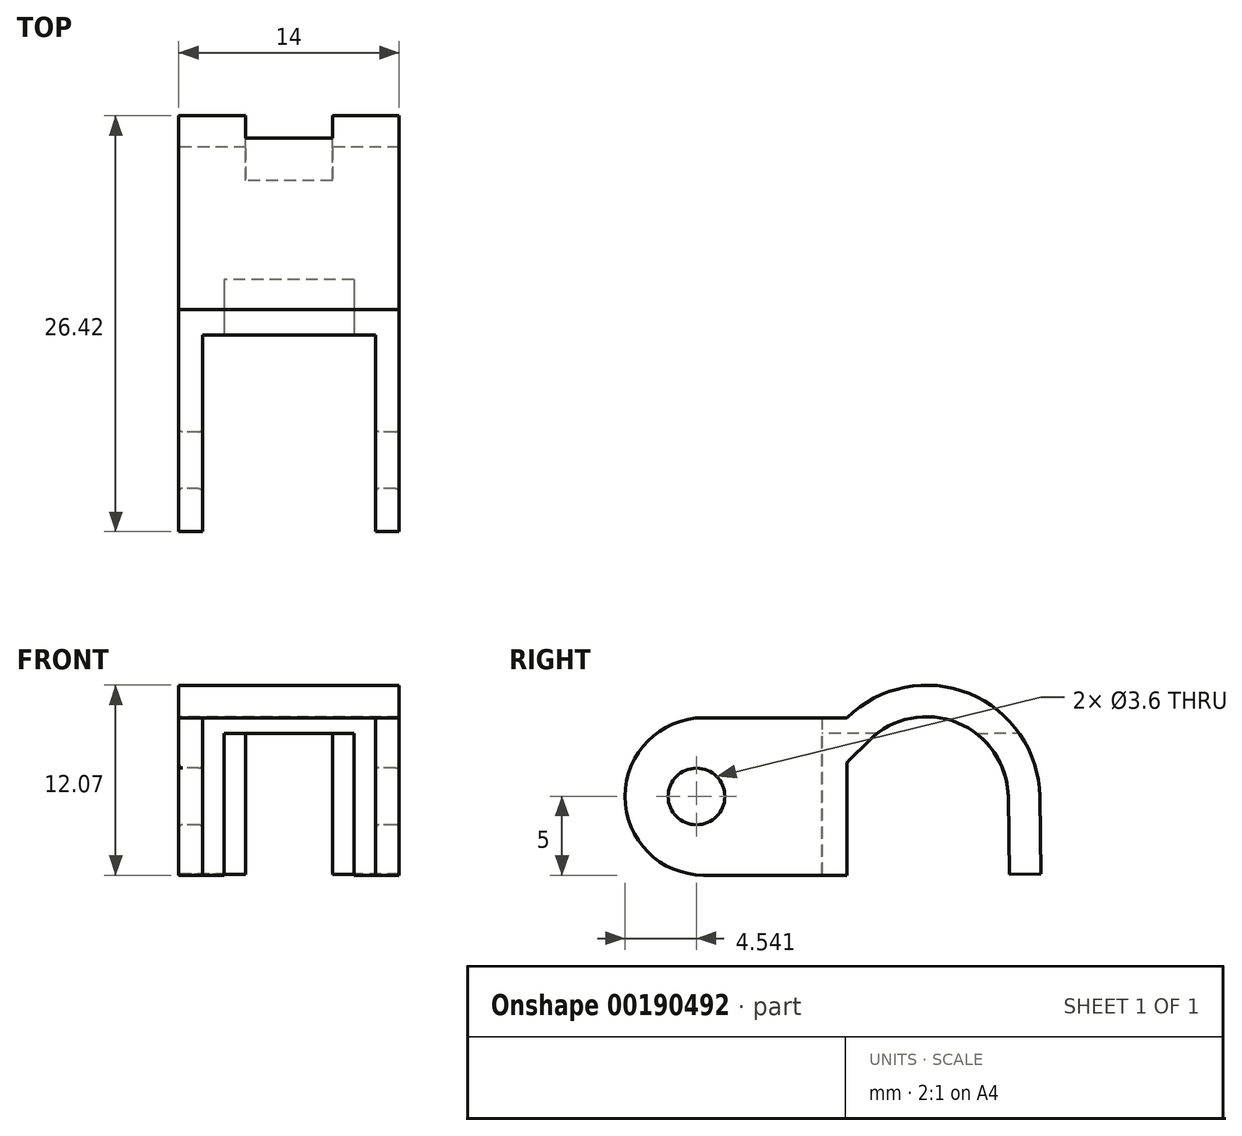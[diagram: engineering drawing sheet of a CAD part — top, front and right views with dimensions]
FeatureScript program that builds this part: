
annotation { "Feature Type Name" : "Feature", "Feature Type Description" : "" }
export const myFeature = defineFeature(function(context is Context, id is Id, definition is map)
    precondition{}
    {
        {
            var Q0;
            Q0=qCreatedBy(makeId("Right.planeOp"),FACE);
            var sketch = newSketch(context, id + "F0", { "sketchPlane" : qUnion([Q0])});
            skLineSegment(sketch, "E0", {"start": v(48.18, 0) * mm, "end": v(-52.58, 0) * mm, "construction": true});
            skLineSegment(sketch, "E1", {"start": v(0, -5) * mm, "end": v(-9.11, -5) * mm});
            skLineSegment(sketch, "E2.MirrorCS", {"start": v(0, 5) * mm, "end": v(-9.11, 5) * mm});
            skArc(sketch, "E3", {"start": v(-9.11, 5) * mm, "mid": v(-14.11, 0) * mm, "end": v(-9.11, -5) * mm});
            skCircle(sketch, "E4", {"center": v(-9.57, 0) * mm, "radius": 1.8 * mm});
            skArc(sketch, "E5", {"start": v(12.23, 0) * mm, "mid": v(7.76, 6.53) * mm, "end": v(0, 5) * mm});
            skLineSegment(sketch, "E6", {"start": v(12.23, 0) * mm, "end": v(12.31, -4.9) * mm});
            skArc(sketch, "E7.0", {"start": v(10.23, -0.03) * mm, "mid": v(7, 4.68) * mm, "end": v(1.4, 3.58) * mm});
            skLineSegment(sketch, "E7.1", {"start": v(10.23, -0.03) * mm, "end": v(10.31, -4.94) * mm});
            skLineSegment(sketch, "E8", {"start": v(1.4, 3.58) * mm, "end": v(0, 2.2) * mm});
            skLineSegment(sketch, "E9", {"start": v(0, -5) * mm, "end": v(0, 2.2) * mm});
            skLineSegment(sketch, "E10", {"start": v(10.31, -4.94) * mm, "end": v(12.31, -4.9) * mm});
            skSolve(sketch);
        }
        {
            var Q0;
            Q0=makeQuery(id+"F0.imprint","IMPRINT",FACE,{"disambiguationData":[TD([[makeQuery(id+"F0.imprint","IMPRINT",EDGE,{"derivedFrom":sQuery(id+"F0.wireOp",EDGE,"E1")}),-1.0]])]});
            extrude(context, id + "F1", {"entities" : qUnion([Q0]), "depth" : 14 * mm});
        }
        {
            var Q0;
            Q0=makeQuery(id+"F1.opExtrude","SWEPT_FACE",FACE,{"disambiguationData":[OSD([sQuery(id+"F0.wireOp",EDGE,"E6")])]});
            var sketch = newSketch(context, id + "F2", { "sketchPlane" : qUnion([Q0])});
            skLineSegment(sketch, "E11.bottom", {"start": v(-9.75, 3.87) * mm, "end": v(-4.25, 3.87) * mm});
            skLineSegment(sketch, "E11.top", {"start": v(-9.75, -14.1) * mm, "end": v(-4.25, -14.1) * mm});
            skLineSegment(sketch, "E11.left", {"start": v(-9.75, 3.87) * mm, "end": v(-9.75, -14.1) * mm});
            skLineSegment(sketch, "E11.right", {"start": v(-4.25, 3.87) * mm, "end": v(-4.25, -14.1) * mm});
            skPoint(sketch, "E11.middle", {"position": v(-7, -5.11) * mm});
            skSolve(sketch);
        }
        {
            var Q0;
            {var subQ0=sQuery(id+"F2.wireOp",EDGE,"E11.bottom");Q0=makeQuery(id+"F2.imprint","IMPRINT",FACE,{"disambiguationData":[TD([[makeQuery(id+"F2.imprint","IMPRINT",EDGE,{"derivedFrom":subQ0}),-1.0]])]});}
            var Q1;
            {var subQ0=sQuery(id+"F2.wireOp",EDGE,"E11.left");var subQ1=sQuery(id+"F0.wireOp",EDGE,"E6");var subQ2=makeQuery(id+"F1.opExtrude","SWEPT_EDGE",EDGE,{"disambiguationData":[OSD([sQuery(id+"F0.wireOp",EDGE,"E5"),subQ1])]});var subQ3=makeQuery(id+"F2.imprint","INTERSECT",VERTEX,{"derivedFrom":[subQ2,subQ0]});Q1=makeQuery(id+"F2.imprint","IMPRINT",FACE,{"disambiguationData":[TD([[makeQuery(id+"F2.imprint","IMPRINT",EDGE,{"disambiguationData":[TD([[subQ3,-1.0]])],"derivedFrom":subQ0}),1.0]])]});}
            extrude(context, id + "F3", {"entities" : qUnion([Q0, Q1]), "operationType" : NewBodyOperationType.REMOVE, "oppositeDirection" : true, "depth" : 5 * mm});
        }
        {
            var Q0;
            Q0=makeQuery(id+"F1.opExtrude","SWEPT_FACE",FACE,{"disambiguationData":[OSD([sQuery(id+"F0.wireOp",EDGE,"E1")])]});
            var sketch = newSketch(context, id + "F4", { "sketchPlane" : qUnion([Q0])});
            skLineSegment(sketch, "E12.bottom", {"start": v(12.5, 1.61) * mm, "end": v(1.5, 1.61) * mm});
            skLineSegment(sketch, "E12.top", {"start": v(12.5, 16.61) * mm, "end": v(1.5, 16.61) * mm});
            skLineSegment(sketch, "E12.left", {"start": v(12.5, 1.61) * mm, "end": v(12.5, 16.61) * mm});
            skLineSegment(sketch, "E12.right", {"start": v(1.5, 1.61) * mm, "end": v(1.5, 16.61) * mm});
            skPoint(sketch, "E12.middle", {"position": v(7, 9.11) * mm});
            skSolve(sketch);
        }
        {
            var Q0;
            {var subQ0=sQuery(id+"F4.wireOp",EDGE,"E12.top");Q0=makeQuery(id+"F4.imprint","IMPRINT",FACE,{"disambiguationData":[TD([[makeQuery(id+"F4.imprint","IMPRINT",EDGE,{"derivedFrom":subQ0}),1.0]])]});}
            var Q1;
            {var subQ0=sQuery(id+"F4.wireOp",EDGE,"E12.left");var subQ1=sQuery(id+"F0.wireOp",EDGE,"E1");var subQ2=makeQuery(id+"F1.opExtrude","SWEPT_EDGE",EDGE,{"disambiguationData":[OSD([subQ1,sQuery(id+"F0.wireOp",EDGE,"E9")])]});var subQ3=makeQuery(id+"F4.imprint","INTERSECT",VERTEX,{"derivedFrom":[subQ2,subQ0]});Q1=makeQuery(id+"F4.imprint","IMPRINT",FACE,{"disambiguationData":[TD([[makeQuery(id+"F4.imprint","IMPRINT",EDGE,{"disambiguationData":[TD([[subQ3,-1.0]])],"derivedFrom":subQ0}),1.0]])]});}
            extrude(context, id + "F5", {"entities" : qUnion([Q0, Q1]), "operationType" : NewBodyOperationType.REMOVE, "oppositeDirection" : true, "depth" : 12 * mm});
        }
        {
            var Q0;
            Q0=makeQuery(id+"F5.boolean.opBoolean","INTERSECT",EDGE,{"derivedFrom":[makeQuery(id+"F1.opExtrude","SWEPT_FACE",FACE,{"disambiguationData":[OSD([sQuery(id+"F0.wireOp",EDGE,"E3")])]}),makeQuery(id+"F5.opExtrude","CAP_FACE",FACE,{"disambiguationData":[OSD([sQuery(id+"F0.wireOp",EDGE,"E1"),sQuery(id+"F0.wireOp",EDGE,"E9"),sQuery(id+"F4.wireOp",EDGE,"E12.top"),sQuery(id+"F4.wireOp",EDGE,"E12.left"),sQuery(id+"F4.wireOp",EDGE,"E12.right")])],"isStart":false})]});
            var Q1;
            Q1=makeQuery(id+"F5.boolean.opBoolean","INTERSECT",EDGE,{"derivedFrom":[makeQuery(id+"F1.opExtrude","SWEPT_FACE",FACE,{"disambiguationData":[OSD([sQuery(id+"F0.wireOp",EDGE,"E4")])]}),makeQuery(id+"F5.opExtrude","SWEPT_FACE",FACE,{"disambiguationData":[OSD([sQuery(id+"F4.wireOp",EDGE,"E12.right")])]})]});
            var Q2;
            Q2=makeQuery(id+"F5.boolean.opBoolean","INTERSECT",EDGE,{"derivedFrom":[makeQuery(id+"F1.opExtrude","SWEPT_FACE",FACE,{"disambiguationData":[OSD([sQuery(id+"F0.wireOp",EDGE,"E4")])]}),makeQuery(id+"F5.opExtrude","SWEPT_FACE",FACE,{"disambiguationData":[OSD([sQuery(id+"F4.wireOp",EDGE,"E12.left")])]})]});
            var Q3;
            Q3=makeQuery(id+"F1.opExtrude","CAP_EDGE",EDGE,{"disambiguationData":[OSD([sQuery(id+"F0.wireOp",EDGE,"E4")])],"isStart":true});
            var Q4;
            Q4=makeQuery(id+"F1.opExtrude","CAP_EDGE",EDGE,{"disambiguationData":[OSD([sQuery(id+"F0.wireOp",EDGE,"E4")])],"isStart":false});
            var Q5;
            {var subQ0=sQuery(id+"F0.wireOp",EDGE,"E9");var subQ1=sQuery(id+"F0.wireOp",EDGE,"E8");var subQ2=sQuery(id+"F0.wireOp",EDGE,"E1");Q5=makeQuery(id+"F5.boolean.opBoolean","SPLIT",EDGE,{"disambiguationData":[TD([makeQuery(id+"F1.opExtrude","CAP_FACE",FACE,{"disambiguationData":[OSD([subQ2,sQuery(id+"F0.wireOp",EDGE,"E2.MirrorCS"),sQuery(id+"F0.wireOp",EDGE,"E3"),sQuery(id+"F0.wireOp",EDGE,"E4"),sQuery(id+"F0.wireOp",EDGE,"E5"),sQuery(id+"F0.wireOp",EDGE,"E6"),sQuery(id+"F0.wireOp",EDGE,"E7.0"),sQuery(id+"F0.wireOp",EDGE,"E7.1"),subQ1,subQ0,sQuery(id+"F0.wireOp",EDGE,"E10")])],"isStart":true}),makeQuery(id+"F1.opExtrude","SWEPT_FACE",FACE,{"disambiguationData":[OSD([subQ1])]}),makeQuery(id+"F1.opExtrude","SWEPT_FACE",FACE,{"disambiguationData":[OSD([subQ0])]}),makeQuery(id+"F5.opExtrude","SWEPT_FACE",FACE,{"disambiguationData":[OSD([sQuery(id+"F4.wireOp",EDGE,"E12.right")])]}),makeQuery(id+"F5.opExtrude","SWEPT_FACE",FACE,{"disambiguationData":[OSD([subQ2,subQ0])]})])],"derivedFrom":makeQuery(id+"F1.opExtrude","SWEPT_EDGE",EDGE,{"disambiguationData":[OSD([subQ1,subQ0])]})});}
            var Q6;
            {var subQ0=sQuery(id+"F0.wireOp",EDGE,"E9");var subQ1=sQuery(id+"F0.wireOp",EDGE,"E8");var subQ2=sQuery(id+"F0.wireOp",EDGE,"E1");Q6=makeQuery(id+"F5.boolean.opBoolean","SPLIT",EDGE,{"disambiguationData":[TD([makeQuery(id+"F1.opExtrude","CAP_FACE",FACE,{"disambiguationData":[OSD([subQ2,sQuery(id+"F0.wireOp",EDGE,"E2.MirrorCS"),sQuery(id+"F0.wireOp",EDGE,"E3"),sQuery(id+"F0.wireOp",EDGE,"E4"),sQuery(id+"F0.wireOp",EDGE,"E5"),sQuery(id+"F0.wireOp",EDGE,"E6"),sQuery(id+"F0.wireOp",EDGE,"E7.0"),sQuery(id+"F0.wireOp",EDGE,"E7.1"),subQ1,subQ0,sQuery(id+"F0.wireOp",EDGE,"E10")])],"isStart":false}),makeQuery(id+"F1.opExtrude","SWEPT_FACE",FACE,{"disambiguationData":[OSD([subQ1])]}),makeQuery(id+"F1.opExtrude","SWEPT_FACE",FACE,{"disambiguationData":[OSD([subQ0])]}),makeQuery(id+"F5.opExtrude","SWEPT_FACE",FACE,{"disambiguationData":[OSD([sQuery(id+"F4.wireOp",EDGE,"E12.left")])]}),makeQuery(id+"F5.opExtrude","SWEPT_FACE",FACE,{"disambiguationData":[OSD([subQ2,subQ0])]})])],"derivedFrom":makeQuery(id+"F1.opExtrude","SWEPT_EDGE",EDGE,{"disambiguationData":[OSD([subQ1,subQ0])]})});}
            fillet(context, id + "F6", {"entities" : qUnion([Q0, Q1, Q2, Q3, Q4, Q5, Q6]), "radius" : 0.23 * mm, "tangentPropagation" : true, "allowEdgeOverflow" : false});
        }
        {
            var Q0;
            Q0=makeQuery(id+"F5.boolean.opBoolean","COPY",FACE,{"derivedFrom":makeQuery(id+"F5.opExtrude","SWEPT_FACE",FACE,{"disambiguationData":[OSD([sQuery(id+"F4.wireOp",EDGE,"E12.bottom")])]})});
            var sketch = newSketch(context, id + "F7", { "sketchPlane" : qUnion([Q0])});
            skLineSegment(sketch, "E13", {"start": v(2.88, -5) * mm, "end": v(2.88, 4.01) * mm});
            skLineSegment(sketch, "E14", {"start": v(7, -6.09) * mm, "end": v(7, 6.49) * mm, "construction": true});
            skPoint(sketch, "E14.startSnap0", {"position": v(7, 5) * mm});
            skLineSegment(sketch, "E15.MirrorCS", {"start": v(11.12, -5) * mm, "end": v(11.12, 4.01) * mm});
            skLineSegment(sketch, "E16", {"start": v(2.88, 4.01) * mm, "end": v(11.12, 4.01) * mm});
            skLineSegment(sketch, "E17", {"start": v(2.88, -5) * mm, "end": v(11.12, -5) * mm});
            skSolve(sketch);
        }
        {
            var Q0;
            Q0=makeQuery(id+"F7.imprint","IMPRINT",FACE,{"disambiguationData":[TD([[makeQuery(id+"F7.imprint","IMPRINT",EDGE,{"derivedFrom":sQuery(id+"F7.wireOp",EDGE,"E13")}),-1.0]])]});
            extrude(context, id + "F8", {"entities" : qUnion([Q0]), "operationType" : NewBodyOperationType.REMOVE, "oppositeDirection" : true, "depth" : 5 * mm});
        }
        {
            var Q0;
            Q0=makeQuery(id+"F1.opExtrude","SWEPT_BODY",BODY,{"disambiguationData":[OSD([sQuery(id+"F0.wireOp",EDGE,"E1"),sQuery(id+"F0.wireOp",EDGE,"E2.MirrorCS"),sQuery(id+"F0.wireOp",EDGE,"E3"),sQuery(id+"F0.wireOp",EDGE,"E4"),sQuery(id+"F0.wireOp",EDGE,"E5"),sQuery(id+"F0.wireOp",EDGE,"E6"),sQuery(id+"F0.wireOp",EDGE,"E7.0"),sQuery(id+"F0.wireOp",EDGE,"E7.1"),sQuery(id+"F0.wireOp",EDGE,"E8"),sQuery(id+"F0.wireOp",EDGE,"E9"),sQuery(id+"F0.wireOp",EDGE,"E10")])]});
            transform(context, id + "F9", {"entities" : qUnion([Q0]), "transformType" : TransformType.TRANSLATION_3D, "dx" : 0 * mm, "dy" : 0 * mm, "dz" : 0 * mm, "makeCopy" : true});
        }
        {
            var Q0;
            Q0=makeQuery(id+"F9.opPattern","COPY",BODY,{"derivedFrom":makeQuery(id+"F1.opExtrude","SWEPT_BODY",BODY,{"disambiguationData":[OSD([sQuery(id+"F0.wireOp",EDGE,"E1"),sQuery(id+"F0.wireOp",EDGE,"E2.MirrorCS"),sQuery(id+"F0.wireOp",EDGE,"E3"),sQuery(id+"F0.wireOp",EDGE,"E4"),sQuery(id+"F0.wireOp",EDGE,"E5"),sQuery(id+"F0.wireOp",EDGE,"E6"),sQuery(id+"F0.wireOp",EDGE,"E7.0"),sQuery(id+"F0.wireOp",EDGE,"E7.1"),sQuery(id+"F0.wireOp",EDGE,"E8"),sQuery(id+"F0.wireOp",EDGE,"E9"),sQuery(id+"F0.wireOp",EDGE,"E10")])]}),"instanceName":"1"});
            deleteBodies(context, id + "F10", {"entities" : qUnion([Q0])});
        }
        {
            var Q0;
            Q0=makeQuery(id+"F1.opExtrude","SWEPT_BODY",BODY,{"disambiguationData":[OSD([sQuery(id+"F0.wireOp",EDGE,"E1"),sQuery(id+"F0.wireOp",EDGE,"E2.MirrorCS"),sQuery(id+"F0.wireOp",EDGE,"E3"),sQuery(id+"F0.wireOp",EDGE,"E4"),sQuery(id+"F0.wireOp",EDGE,"E5"),sQuery(id+"F0.wireOp",EDGE,"E6"),sQuery(id+"F0.wireOp",EDGE,"E7.0"),sQuery(id+"F0.wireOp",EDGE,"E7.1"),sQuery(id+"F0.wireOp",EDGE,"E8"),sQuery(id+"F0.wireOp",EDGE,"E9"),sQuery(id+"F0.wireOp",EDGE,"E10")])]});
            transform(context, id + "F11", {"entities" : qUnion([Q0]), "transformType" : TransformType.TRANSLATION_3D, "dx" : 0 * mm, "dy" : 0 * mm, "dz" : 0 * mm, "makeCopy" : true});
        }
        {
            var Q0;
            Q0=makeQuery(id+"F11.opPattern","COPY",BODY,{"derivedFrom":makeQuery(id+"F1.opExtrude","SWEPT_BODY",BODY,{"disambiguationData":[OSD([sQuery(id+"F0.wireOp",EDGE,"E1"),sQuery(id+"F0.wireOp",EDGE,"E2.MirrorCS"),sQuery(id+"F0.wireOp",EDGE,"E3"),sQuery(id+"F0.wireOp",EDGE,"E4"),sQuery(id+"F0.wireOp",EDGE,"E5"),sQuery(id+"F0.wireOp",EDGE,"E6"),sQuery(id+"F0.wireOp",EDGE,"E7.0"),sQuery(id+"F0.wireOp",EDGE,"E7.1"),sQuery(id+"F0.wireOp",EDGE,"E8"),sQuery(id+"F0.wireOp",EDGE,"E9"),sQuery(id+"F0.wireOp",EDGE,"E10")])]}),"instanceName":"1"});
            deleteBodies(context, id + "F12", {"entities" : qUnion([Q0])});
        }
    });
